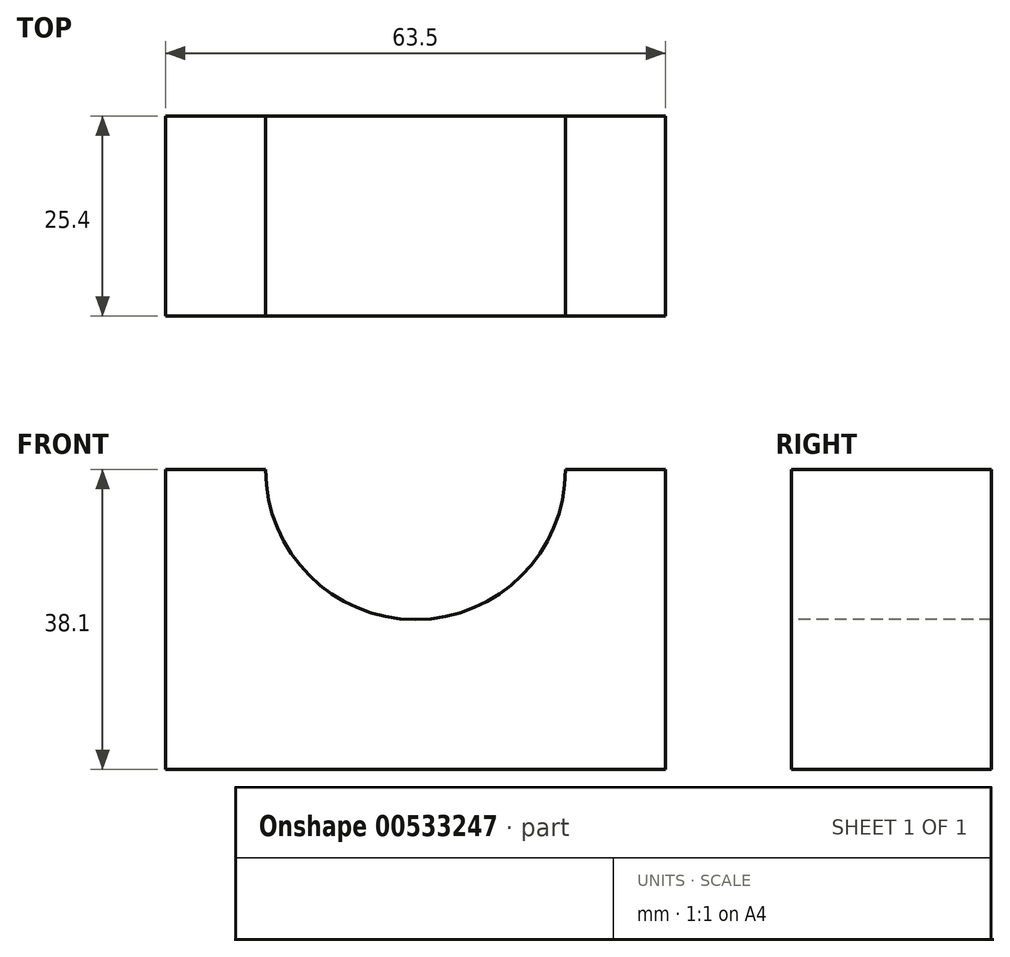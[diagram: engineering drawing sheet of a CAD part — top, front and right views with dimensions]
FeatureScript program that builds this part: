
annotation { "Feature Type Name" : "Feature", "Feature Type Description" : "" }
export const myFeature = defineFeature(function(context is Context, id is Id, definition is map)
    precondition{}
    {
        {
            var Q0;
            Q0=qCreatedBy(makeId("Front.planeOp"),FACE);
            var sketch = newSketch(context, id + "F0", { "sketchPlane" : qUnion([Q0])});
            skLineSegment(sketch, "E0.bottom", {"start": v(0, 0) * mm, "end": v(63.5, 0) * mm});
            skLineSegment(sketch, "E0.top", {"start": v(0, 38.1) * mm, "end": v(63.5, 38.1) * mm});
            skLineSegment(sketch, "E0.left", {"start": v(0, 0) * mm, "end": v(0, 38.1) * mm});
            skLineSegment(sketch, "E0.right", {"start": v(63.5, 0) * mm, "end": v(63.5, 38.1) * mm});
            skSolve(sketch);
        }
        {
            var Q0;
            Q0=makeQuery(id+"F0.imprint","IMPRINT",FACE,{"disambiguationData":[TD([[makeQuery(id+"F0.imprint","IMPRINT",EDGE,{"derivedFrom":sQuery(id+"F0.wireOp",EDGE,"E0.bottom")}),1.0]])]});
            extrude(context, id + "F1", {"entities" : qUnion([Q0]), "depth" : 25.4 * mm, "offsetDistance" : 25.4 * mm});
        }
        {
            var Q0;
            Q0=makeQuery(id+"F1.opExtrude","CAP_FACE",FACE,{"disambiguationData":[OSD([sQuery(id+"F0.wireOp",EDGE,"E0.bottom"),sQuery(id+"F0.wireOp",EDGE,"E0.top"),sQuery(id+"F0.wireOp",EDGE,"E0.left"),sQuery(id+"F0.wireOp",EDGE,"E0.right")])],"isStart":false});
            var sketch = newSketch(context, id + "F2", { "sketchPlane" : qUnion([Q0])});
            skLineSegment(sketch, "E1", {"start": v(0, 38.1) * mm, "end": v(63.5, 38.1) * mm});
            skArc(sketch, "E2", {"start": v(12.7, 38.1) * mm, "mid": v(31.75, 19.05) * mm, "end": v(50.8, 38.1) * mm});
            skSolve(sketch);
        }
        {
            var Q0;
            {var subQ0=sQuery(id+"F2.wireOp",EDGE,"E2");Q0=makeQuery(id+"F2.imprint","IMPRINT",FACE,{"disambiguationData":[TD([[makeQuery(id+"F2.imprint","IMPRINT",EDGE,{"derivedFrom":subQ0}),1.0]])]});}
            extrude(context, id + "F3", {"entities" : qUnion([Q0]), "operationType" : NewBodyOperationType.REMOVE, "oppositeDirection" : true, "depth" : 25.4 * mm, "offsetDistance" : 25.4 * mm});
        }
    });
